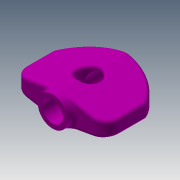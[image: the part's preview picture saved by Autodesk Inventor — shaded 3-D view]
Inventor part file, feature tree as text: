
AUTODESK INVENTOR PART (.ipt)
format: ipt  version: 2014 (Build 180170000, 170)  size: 355,840 bytes
history: native  units: mm (DEFAULTED — no unit token found)
features: sketch x4, extrude x4, fillet x4, plane x1
ambient origin geometry x8: Origin, YZ Plane, XZ Plane, XY Plane, X Axis, Y Axis, Z Axis, Center Point
bodies: Solid1 (feature_tree)
feature tree (13):
  sketch  "Sketch1"  dims[d2=3.175mm d3=0.0mm d4=15.875mm d5=0.0mm]
  plane  "Work Plane1"
  sketch  "Sketch2"  dims[d6=3.175mm d7=0.762mm d8=15.875mm d9=0.0mm d10=0.762mm]
  extrude  "Extrusion1"  Depth=15.875mm TaperAngle=0.0deg
  extrude  "Extrusion2"  Depth=0.762mm
  fillet  "Fillet1"  Radius=15.875mm
  fillet  "Fillet2"  Radius=0.762mm
  extrude  "Extrusion3"  Depth=3.175mm
  fillet  "Fillet3"  Radius=25.4mm
  extrude  "Extrusion4"  [1 undecoded]
  fillet  "Fillet4"  [1 undecoded]
  sketch  "Sketch3"  dims[d12=3.175mm d13=3.175mm d14=25.4mm d15=0.0mm]
  sketch  "Sketch5"  dims[d16=0.635mm]
note: 2 required parameter values undecoded (feature->parameter linkage not recoverable at this tier; creation-order binding heuristic only, values carry confidence <= 0.55)
